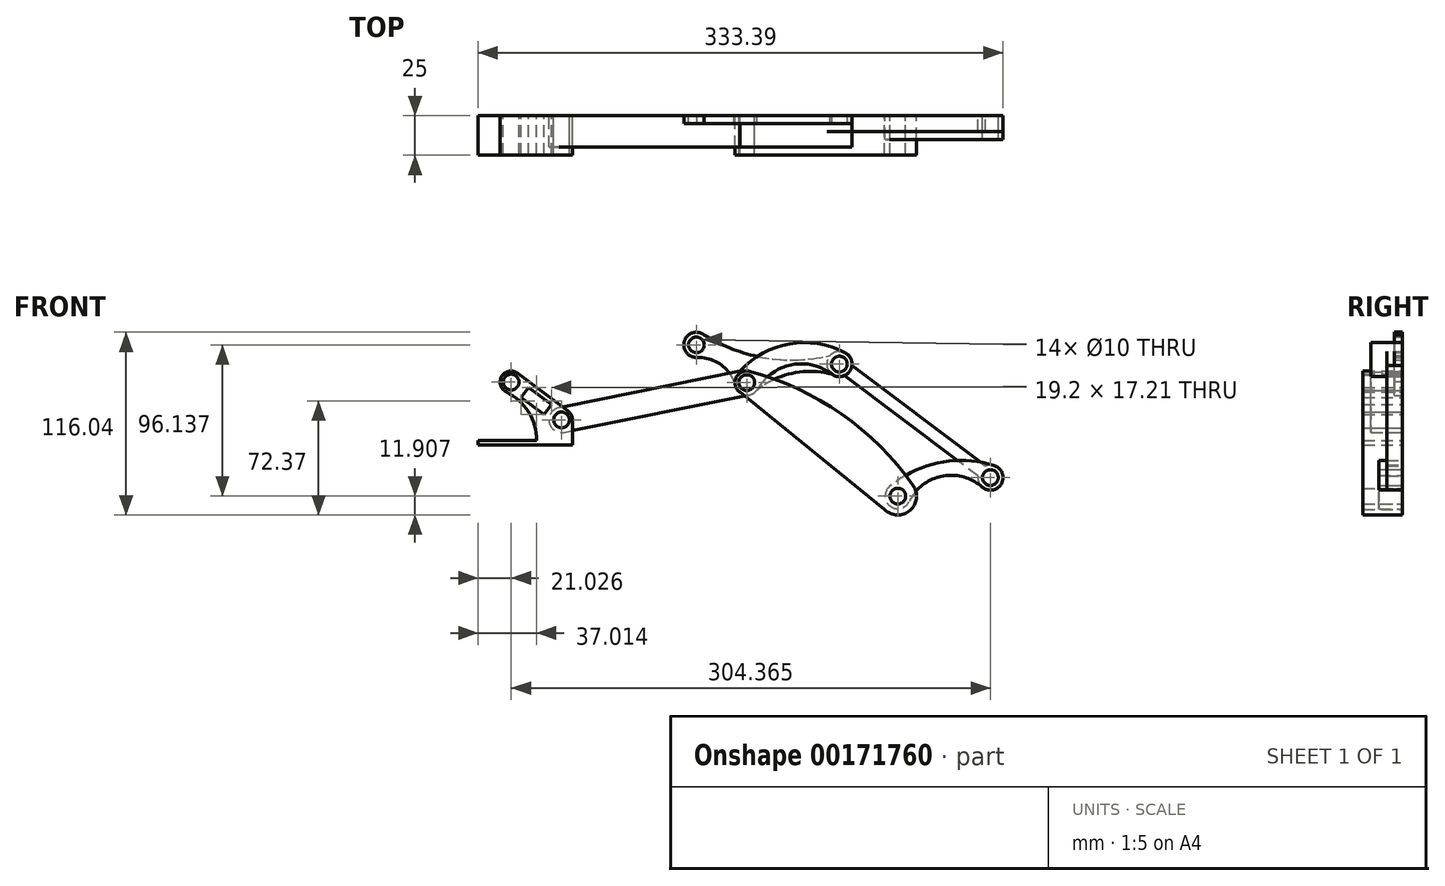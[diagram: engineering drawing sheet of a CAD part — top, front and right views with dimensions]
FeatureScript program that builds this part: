
annotation { "Feature Type Name" : "Feature", "Feature Type Description" : "" }
export const myFeature = defineFeature(function(context is Context, id is Id, definition is map)
    precondition{}
    {
        {
            var Q0;
            Q0=qCreatedBy(makeId("Front.planeOp"),FACE);
            var sketch = newSketch(context, id + "F0", { "sketchPlane" : qUnion([Q0])});
            skCircle(sketch, "E0", {"center": v(19.37, 16.2) * mm, "radius": 5 * mm});
            skArc(sketch, "E1", {"start": v(29.13, 23.02) * mm, "mid": v(-16.33, 68.47) * mm, "end": v(-74.66, 95.5) * mm});
            skCircle(sketch, "E2", {"center": v(-76.55, 88.3) * mm, "radius": 5 * mm});
            skLineSegment(sketch, "E3", {"start": v(-81.52, 82.78) * mm, "end": v(12.77, 6.3) * mm});
            skArc(sketch, "E4", {"start": v(11.04, 7.7) * mm, "mid": v(27.06, 7.12) * mm, "end": v(29.13, 23.02) * mm});
            skArc(sketch, "E5", {"start": v(-74.66, 95.5) * mm, "mid": v(-83.27, 91.5) * mm, "end": v(-80.94, 82.3) * mm});
            skSolve(sketch);
        }
        {
            var Q0;
            Q0=qCreatedBy(makeId("Front.planeOp"),FACE);
            var sketch = newSketch(context, id + "F1", { "sketchPlane" : qUnion([Q0])});
            skCircle(sketch, "E6.0", {"center": v(-76.55, 88.3) * mm, "radius": 5 * mm});
            skCircle(sketch, "E7", {"center": v(-194.2, 64.65) * mm, "radius": 5 * mm});
            skCircle(sketch, "E8", {"center": v(-194.2, 64.65) * mm, "radius": 8 * mm});
            skCircle(sketch, "E9", {"center": v(-76.55, 88.3) * mm, "radius": 8 * mm});
            skLineSegment(sketch, "E10", {"start": v(-192.62, 56.81) * mm, "end": v(-74.98, 80.47) * mm});
            skLineSegment(sketch, "E11", {"start": v(-195.78, 72.5) * mm, "end": v(-78.13, 96.15) * mm});
            skLineSegment(sketch, "E12", {"start": v(-194.2, 64.65) * mm, "end": v(15, 106.72) * mm, "construction": true});
            skCircle(sketch, "E13", {"center": v(-17.73, 100.14) * mm, "radius": 5 * mm});
            skCircle(sketch, "E14", {"center": v(-17.73, 100.14) * mm, "radius": 8 * mm});
            skArc(sketch, "E15", {"start": v(-22.57, 93.76) * mm, "mid": v(-48.23, 99.64) * mm, "end": v(-69.63, 84.3) * mm});
            skArc(sketch, "E16", {"start": v(-13.95, 107.18) * mm, "mid": v(-50.85, 112.66) * mm, "end": v(-82.77, 93.35) * mm});
            skSolve(sketch);
        }
        {
            var Q0;
            Q0=qCreatedBy(makeId("Front.planeOp"),FACE);
            var sketch = newSketch(context, id + "F2", { "sketchPlane" : qUnion([Q0])});
            skCircle(sketch, "E17.0", {"center": v(-17.73, 100.14) * mm, "radius": 5 * mm});
            skCircle(sketch, "E18.0", {"center": v(19.37, 16.2) * mm, "radius": 5 * mm});
            skLineSegment(sketch, "E19.0", {"start": v(-194.2, 64.65) * mm, "end": v(15, 106.72) * mm, "construction": true});
            skLineSegment(sketch, "E20", {"start": v(19.37, 16.2) * mm, "end": v(161.68, 44.82) * mm, "construction": true});
            skCircle(sketch, "E21", {"center": v(78.2, 28.04) * mm, "radius": 5 * mm});
            skCircle(sketch, "E22", {"center": v(78.2, 28.04) * mm, "radius": 8 * mm});
            skCircle(sketch, "E23.0", {"center": v(-76.55, 88.3) * mm, "radius": 5 * mm});
            skLineSegment(sketch, "E24", {"start": v(-76.55, 88.3) * mm, "end": v(19.37, 16.2) * mm, "construction": true});
            skLineSegment(sketch, "E25", {"start": v(-17.73, 100.14) * mm, "end": v(116.4, -0.7) * mm, "construction": true});
            skCircle(sketch, "E26", {"center": v(-17.73, 100.14) * mm, "radius": 8 * mm});
            skLineSegment(sketch, "E27", {"start": v(70.25, 29) * mm, "end": v(-14.6, 92.78) * mm});
            skLineSegment(sketch, "E28", {"start": v(-9.79, 99.17) * mm, "end": v(75.06, 35.4) * mm});
            skSolve(sketch);
        }
        {
            var Q0;
            Q0=qCreatedBy(makeId("Front.planeOp"),FACE);
            var sketch = newSketch(context, id + "F3", { "sketchPlane" : qUnion([Q0])});
            skCircle(sketch, "E29.0", {"center": v(19.37, 16.2) * mm, "radius": 5 * mm});
            skCircle(sketch, "E30.0", {"center": v(78.2, 28.04) * mm, "radius": 5 * mm});
            skCircle(sketch, "E31.0", {"center": v(78.2, 28.04) * mm, "radius": 8 * mm});
            skCircle(sketch, "E32", {"center": v(19.37, 16.2) * mm, "radius": 8 * mm});
            skArc(sketch, "E33", {"start": v(80.57, 35.67) * mm, "mid": v(45.7, 37.48) * mm, "end": v(14.22, 22.33) * mm});
            skArc(sketch, "E34", {"start": v(72.88, 22.05) * mm, "mid": v(47.4, 28.94) * mm, "end": v(26.58, 12.74) * mm});
            skSolve(sketch);
        }
        {
            var Q0;
            Q0 = qSketchRegion(id + "F0", true);
            extrude(context, id + "F4", {"entities" : qUnion([Q0]), "depth" : 25 * mm});
        }
        {
            var Q0;
            Q0 = qSketchRegion(id + "F1", true);
            extrude(context, id + "F5", {"entities" : qUnion([Q0]), "depth" : 20 * mm});
        }
        {
            var Q0;
            Q0=makeQuery(id+"F2.imprint","IMPRINT",FACE,{"disambiguationData":[TD([[makeQuery(id+"F2.imprint","IMPRINT",EDGE,{"derivedFrom":sQuery(id+"F2.wireOp",EDGE,"E17.0")}),-1.0]])]});
            var Q1;
            Q1=makeQuery(id+"F2.imprint","IMPRINT",FACE,{"disambiguationData":[TD([[makeQuery(id+"F2.imprint","IMPRINT",EDGE,{"derivedFrom":sQuery(id+"F2.wireOp",EDGE,"E21")}),-1.0]])]});
            var Q2;
            {var subQ0=sQuery(id+"F2.wireOp",EDGE,"E27");Q2=makeQuery(id+"F2.imprint","IMPRINT",FACE,{"disambiguationData":[TD([[makeQuery(id+"F2.imprint","IMPRINT",EDGE,{"derivedFrom":subQ0}),-1.0]])]});}
            extrude(context, id + "F6", {"entities" : qUnion([Q0, Q1, Q2]), "depth" : 10 * mm});
        }
        {
            var Q0;
            Q0 = qSketchRegion(id + "F3", true);
            extrude(context, id + "F7", {"entities" : qUnion([Q0]), "depth" : 15 * mm});
        }
        {
            var Q0;
            Q0=qCreatedBy(makeId("Front.planeOp"),FACE);
            var sketch = newSketch(context, id + "F8", { "sketchPlane" : qUnion([Q0])});
            skCircle(sketch, "E35.0", {"center": v(-76.55, 88.3) * mm, "radius": 5 * mm});
            skLineSegment(sketch, "E36.0", {"start": v(-194.2, 64.65) * mm, "end": v(15, 106.72) * mm, "construction": true});
            skCircle(sketch, "E37.0", {"center": v(78.2, 28.04) * mm, "radius": 5 * mm});
            skCircle(sketch, "E38.0", {"center": v(-17.73, 100.14) * mm, "radius": 5 * mm});
            skLineSegment(sketch, "E39.0", {"start": v(-76.55, 88.3) * mm, "end": v(19.37, 16.2) * mm, "construction": true});
            skLineSegment(sketch, "E40", {"start": v(-76.55, 88.3) * mm, "end": v(-124.87, 124.63) * mm, "construction": true});
            skCircle(sketch, "E41", {"center": v(-108.53, 112.34) * mm, "radius": 5 * mm});
            skCircle(sketch, "E42", {"center": v(-108.53, 112.34) * mm, "radius": 8 * mm});
            skCircle(sketch, "E43", {"center": v(-76.55, 88.3) * mm, "radius": 8 * mm});
            skArc(sketch, "E44", {"start": v(-84.5, 89.18) * mm, "mid": v(-93.92, 100.4) * mm, "end": v(-108.03, 104.36) * mm});
            skCircle(sketch, "E45", {"center": v(-17.73, 100.14) * mm, "radius": 8 * mm});
            skArc(sketch, "E46", {"start": v(-22.44, 93.67) * mm, "mid": v(-47.51, 94.28) * mm, "end": v(-70.16, 83.5) * mm});
            skArc(sketch, "E47", {"start": v(-103.65, 118.68) * mm, "mid": v(-65, 104.07) * mm, "end": v(-23.7, 105.47) * mm});
            skSolve(sketch);
        }
        {
            var Q0;
            {var subQ3=sQuery(id+"F8.wireOp",EDGE,"E44");Q0=makeQuery(id+"F8.imprint","IMPRINT",FACE,{"disambiguationData":[TD([[makeQuery(id+"F8.imprint","IMPRINT",EDGE,{"derivedFrom":subQ3}),-1.0]])]});}
            var Q1;
            Q1=makeQuery(id+"F8.imprint","IMPRINT",FACE,{"disambiguationData":[TD([[makeQuery(id+"F8.imprint","IMPRINT",EDGE,{"derivedFrom":sQuery(id+"F8.wireOp",EDGE,"E41")}),-1.0]])]});
            var Q2;
            Q2=makeQuery(id+"F8.imprint","IMPRINT",FACE,{"disambiguationData":[TD([[makeQuery(id+"F8.imprint","IMPRINT",EDGE,{"derivedFrom":sQuery(id+"F8.wireOp",EDGE,"E35.0")}),-1.0]])]});
            var Q3;
            Q3=makeQuery(id+"F8.imprint","IMPRINT",FACE,{"disambiguationData":[TD([[makeQuery(id+"F8.imprint","IMPRINT",EDGE,{"derivedFrom":sQuery(id+"F8.wireOp",EDGE,"E38.0")}),-1.0]])]});
            extrude(context, id + "F9", {"entities" : qUnion([Q0, Q1, Q2, Q3]), "depth" : 5 * mm});
        }
        {
            var Q0;
            Q0=qCreatedBy(makeId("Front.planeOp"),FACE);
            var sketch = newSketch(context, id + "F10", { "sketchPlane" : qUnion([Q0])});
            skLineSegment(sketch, "E48.0", {"start": v(-194.2, 64.65) * mm, "end": v(15, 106.72) * mm, "construction": true});
            skCircle(sketch, "E49.0", {"center": v(-194.2, 64.65) * mm, "radius": 5 * mm});
            skLineSegment(sketch, "E50.0", {"start": v(-76.55, 88.3) * mm, "end": v(-124.87, 124.63) * mm, "construction": true});
            skCircle(sketch, "E51.0", {"center": v(-108.53, 112.34) * mm, "radius": 5 * mm});
            skCircle(sketch, "E52.0", {"center": v(-76.55, 88.3) * mm, "radius": 5 * mm});
            skLineSegment(sketch, "E53", {"start": v(-194.2, 64.65) * mm, "end": v(-226.17, 88.69) * mm, "construction": true});
            skCircle(sketch, "E54", {"center": v(-226.17, 88.69) * mm, "radius": 5 * mm});
            skCircle(sketch, "E55", {"center": v(-226.17, 88.69) * mm, "radius": 7 * mm});
            skLineSegment(sketch, "E56.bottom", {"start": v(-187.2, 51.65) * mm, "end": v(-247.2, 51.65) * mm});
            skLineSegment(sketch, "E56.top", {"start": v(-187.2, 48.65) * mm, "end": v(-247.2, 48.65) * mm});
            skLineSegment(sketch, "E56.left", {"start": v(-187.2, 51.65) * mm, "end": v(-187.2, 48.65) * mm});
            skLineSegment(sketch, "E56.right", {"start": v(-247.2, 51.65) * mm, "end": v(-247.2, 48.65) * mm});
            skCircle(sketch, "E57", {"center": v(-194.2, 64.65) * mm, "radius": 7 * mm});
            skLineSegment(sketch, "E58", {"start": v(-187.2, 51.65) * mm, "end": v(-187.2, 64.65) * mm});
            skLineSegment(sketch, "E59", {"start": v(-190, 70.25) * mm, "end": v(-221.97, 94.28) * mm});
            skArc(sketch, "E60", {"start": v(-210.01, 51.65) * mm, "mid": v(-215.21, 69.78) * mm, "end": v(-229.24, 82.4) * mm});
            skLineSegment(sketch, "E61", {"start": v(-205.4, 68.07) * mm, "end": v(-200.59, 74.46) * mm});
            skLineSegment(sketch, "E62", {"start": v(-200.59, 74.46) * mm, "end": v(-214.98, 85.28) * mm});
            skLineSegment(sketch, "E63", {"start": v(-214.98, 85.28) * mm, "end": v(-219.78, 78.88) * mm});
            skLineSegment(sketch, "E64", {"start": v(-219.78, 78.88) * mm, "end": v(-205.4, 68.07) * mm});
            skSolve(sketch);
        }
        {
            var Q0;
            Q0=makeQuery(id+"F10.imprint","IMPRINT",FACE,{"disambiguationData":[TD([[makeQuery(id+"F10.imprint","IMPRINT",EDGE,{"derivedFrom":sQuery(id+"F10.wireOp",EDGE,"E54")}),-1.0]])]});
            var Q1;
            {var subQ0=sQuery(id+"F10.wireOp",EDGE,"E58");Q1=makeQuery(id+"F10.imprint","IMPRINT",FACE,{"disambiguationData":[TD([[makeQuery(id+"F10.imprint","IMPRINT",EDGE,{"derivedFrom":subQ0}),1.0]])]});}
            var Q2;
            Q2=makeQuery(id+"F10.imprint","IMPRINT",FACE,{"disambiguationData":[TD([[makeQuery(id+"F10.imprint","IMPRINT",EDGE,{"derivedFrom":sQuery(id+"F10.wireOp",EDGE,"E49.0")}),-1.0]])]});
            var Q3;
            Q3=makeQuery(id+"F10.imprint","IMPRINT",FACE,{"disambiguationData":[TD([[makeQuery(id+"F10.imprint","IMPRINT",EDGE,{"derivedFrom":sQuery(id+"F10.wireOp",EDGE,"E56.top")}),-1.0]])]});
            extrude(context, id + "F11", {"entities" : qUnion([Q0, Q1, Q2, Q3]), "depth" : 25 * mm});
        }
    });
